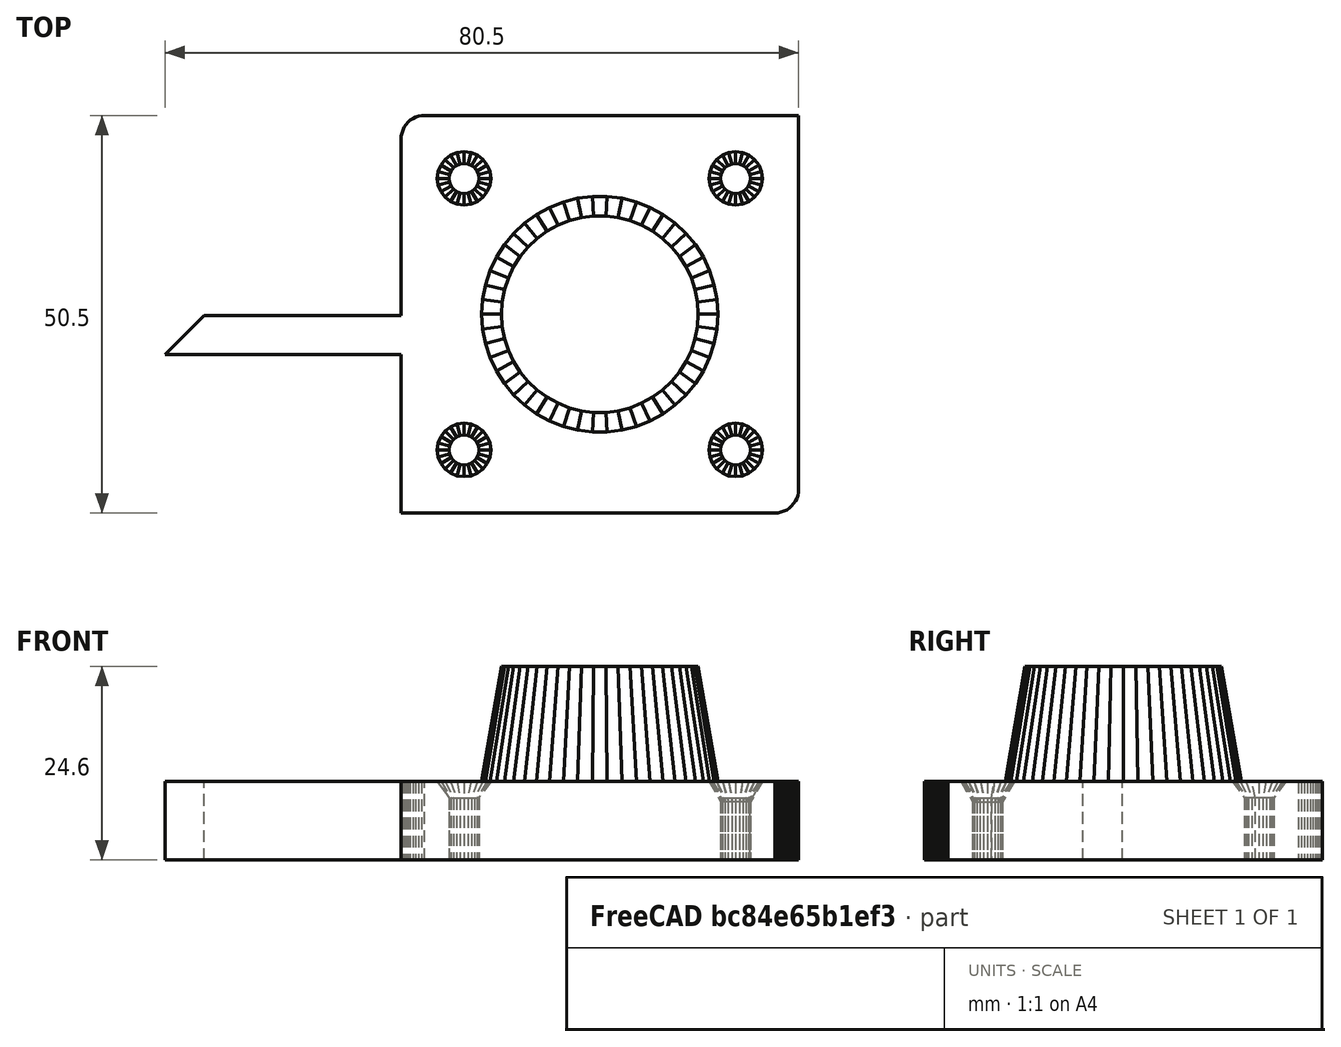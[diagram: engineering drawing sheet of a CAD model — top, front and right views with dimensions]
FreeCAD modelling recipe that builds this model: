
FCSTD DOCUMENT  (FreeCAD 0.17R13541 (Git))
Label: base front right
License: All rights reserved
LicenseURL: http://en.wikipedia.org/wiki/All_rights_reserved
objects: Part::Feature×4, Part::Box×2, Part::Cut×2
note: 8 computed .brp shape members not serialized (recipe doc carries the construction recipe); baked Part::Feature solids carry a one-line shape summary decoded from their .brp

FEATURE [Part::Feature] Solid
  shape: bbox 80.5 x 80.5 x 24.6 mm, 410 faces (baked)
FEATURE [Part::Box] Box  label="Cube"
  AttacherType = Attacher::AttachEngine3D
  Height = 100
  Length = 100
  Placement = pos=(0,50.5,0) rot=(0,0,1;0rad)
  Width = 100
FEATURE [Part::Cut] Cut
  Base = -> Solid
  Tool = -> Box
FEATURE [Part::Box] Box001  label="Cube001"
  AttacherType = Attacher::AttachEngine3D
  Height = 500
  Length = 300
  Placement = pos=(-100,-1,-10) rot=(0,0,1;0rad)
  Width = 51.51
FEATURE [Part::Feature] Base_rear_left_3mm_Perspex001
  Placement = pos=(50.5,0,0) rot=(0,0,1;1.5708rad)
  shape: bbox 80.5 x 80.5 x 24.6 mm, 948 faces, 0 solids (baked)
FEATURE [Part::Cut] Cut001
  Base = -> Base_rear_left_3mm_Perspex001
  Tool = -> Box001
FEATURE [Part::Feature] Cut001001  label="Cut002"
  shape: bbox 13 x 29.99 x 10 mm, 10 faces, 0 solids (baked)
FEATURE [Part::Feature] Cut_rev  label="Cut (Rev)"
  shape: bbox 80.5 x 50.5 x 24.6 mm, 408 faces (baked)
